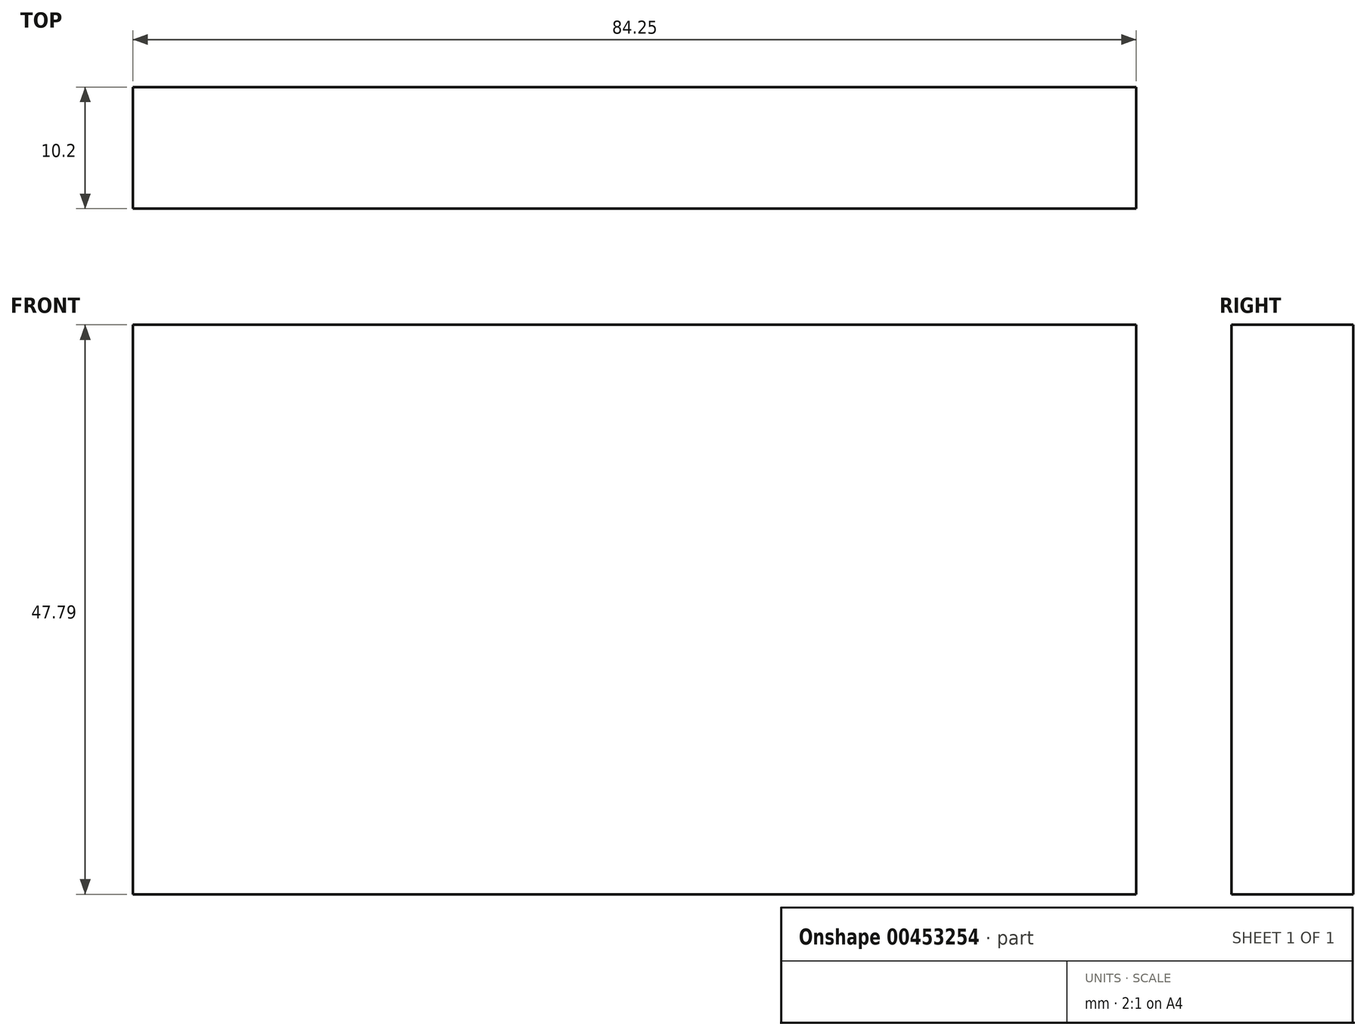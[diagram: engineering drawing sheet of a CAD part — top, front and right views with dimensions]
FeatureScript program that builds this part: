
annotation { "Feature Type Name" : "Feature", "Feature Type Description" : "" }
export const myFeature = defineFeature(function(context is Context, id is Id, definition is map)
    precondition{}
    {
        {
            var Q0;
            Q0=qCreatedBy(makeId("Front.planeOp"),FACE);
            var sketch = newSketch(context, id + "F0", { "sketchPlane" : qUnion([Q0])});
            skLineSegment(sketch, "E0.bottom", {"start": v(-37.77, 17.98) * mm, "end": v(46.48, 17.98) * mm});
            skLineSegment(sketch, "E0.top", {"start": v(-37.77, -29.8) * mm, "end": v(46.48, -29.8) * mm});
            skLineSegment(sketch, "E0.left", {"start": v(-37.77, 17.98) * mm, "end": v(-37.77, -29.8) * mm});
            skLineSegment(sketch, "E0.right", {"start": v(46.48, 17.98) * mm, "end": v(46.48, -29.8) * mm});
            skSolve(sketch);
        }
        {
            var Q0;
            Q0 = qSketchRegion(id + "F0", true);
            extrude(context, id + "F1", {"entities" : qUnion([Q0]), "depth" : 10.2 * mm});
        }
    });
